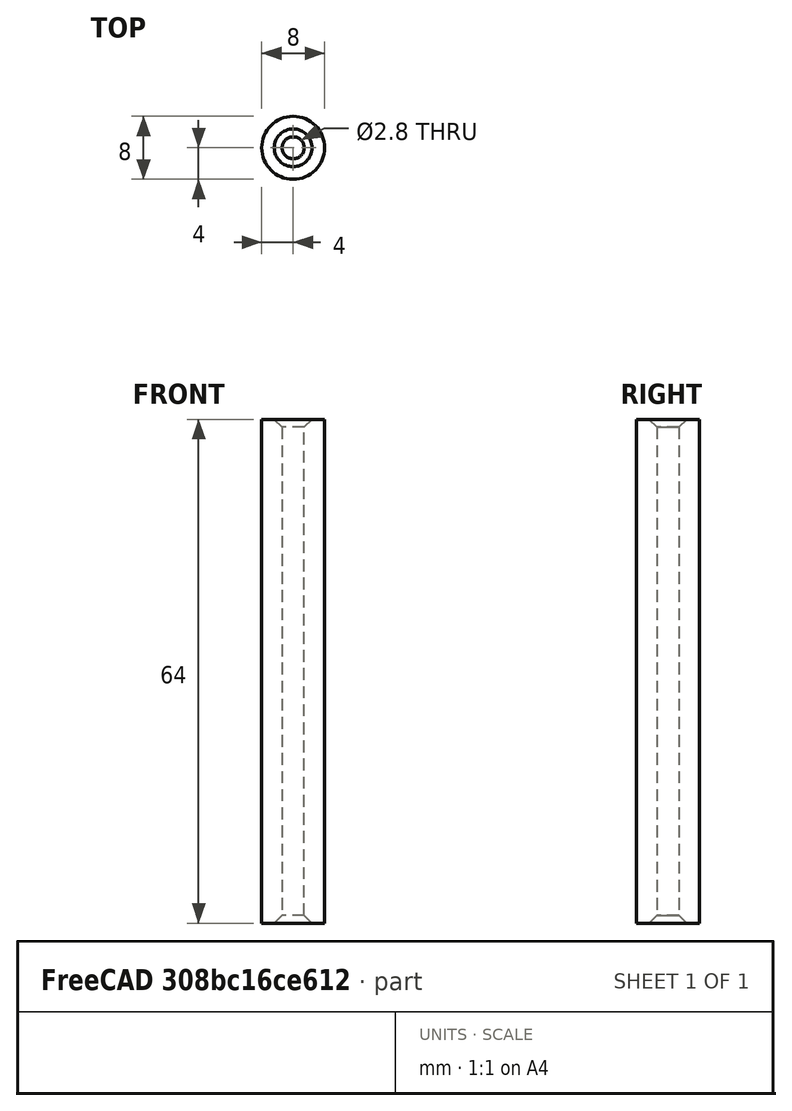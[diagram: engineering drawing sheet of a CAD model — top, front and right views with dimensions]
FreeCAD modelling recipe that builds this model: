
FCSTD DOCUMENT  (FreeCAD 1.0R39109 (Git))
Label: 2_8x8x64mm_spacer
License: All rights reserved
LicenseURL: https://en.wikipedia.org/wiki/All_rights_reserved
objects: Sketcher::SketchObject×1, PartDesign::Pad×1, PartDesign::Chamfer×1, PartDesign::Body×1
note: 9 computed .brp shape members not serialized (recipe doc carries the construction recipe); baked Part::Feature solids carry a one-line shape summary decoded from their .brp

FEATURE [Sketcher::SketchObject] Sketch
  ArcFitTolerance = 1e-06
  AttachmentSupport = -> [XY_Plane]
  FullyConstrained = true
  MakeInternals = false
  MapMode = 5
  sketch-geometry (2):
    g0: Circle CenterX=0 CenterY=0 CenterZ=0 NormalX=0 NormalY=0 NormalZ=1 AngleXU=0 Radius=1.4
    g1: Circle CenterX=0 CenterY=0 CenterZ=0 NormalX=0 NormalY=0 NormalZ=1 AngleXU=0 Radius=4
  constraints (4):
    c: Coincident(g0,g-1)
    c: Coincident(g1,g0)
    c: Diameter(g0) = 2.8
    c: Diameter(g1) = 8
FEATURE [PartDesign::Pad] Pad
  Direction = (0,0,1)
  Length = 64
  Length2 = 10
  Profile = -> Sketch
  ReferenceAxis = -> Sketch [N_Axis]
  Refine = true
  Suppressed = false
  Type = 0
FEATURE [PartDesign::Chamfer] Chamfer
  Angle = 45
  Base = -> Pad [Edge6,Edge5]
  BaseFeature = -> Pad
  ChamferType = 0
  FlipDirection = false
  Refine = true
  Size = 1
  Size2 = 1
  SupportTransform = false
  Suppressed = false
  UseAllEdges = false
FEATURE [PartDesign::Body] Body
  AllowCompound = false
  Group = -> [Sketch,Pad,Chamfer]
  Origin = -> Origin
  Tip = -> Chamfer
